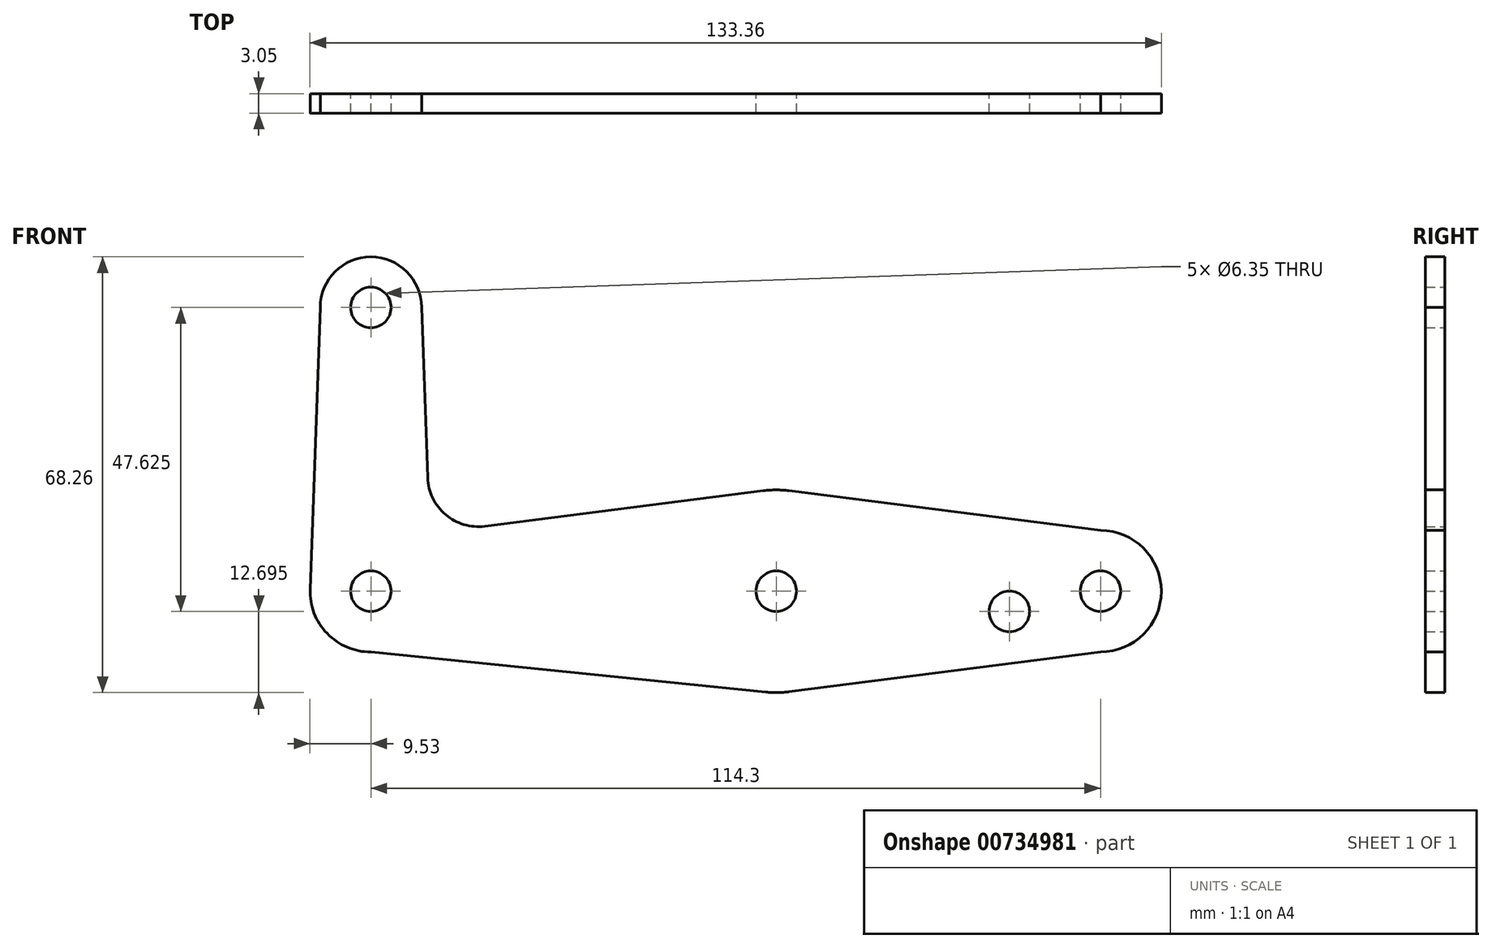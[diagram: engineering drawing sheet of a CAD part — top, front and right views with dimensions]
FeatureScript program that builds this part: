
annotation { "Feature Type Name" : "Feature", "Feature Type Description" : "" }
export const myFeature = defineFeature(function(context is Context, id is Id, definition is map)
    precondition{}
    {
        {
            var Q0;
            Q0=qCreatedBy(makeId("Front.planeOp"),FACE);
            var sketch = newSketch(context, id + "F0", { "sketchPlane" : qUnion([Q0])});
            skLineSegment(sketch, "E0", {"start": v(0, 0) * mm, "end": v(0, 44.45) * mm, "construction": true});
            skLineSegment(sketch, "E1", {"start": v(0, 0) * mm, "end": v(114.3, 0) * mm, "construction": true});
            skCircle(sketch, "E2", {"center": v(0, 44.45) * mm, "radius": 7.94 * mm});
            skCircle(sketch, "E3", {"center": v(0, 0) * mm, "radius": 9.53 * mm});
            skCircle(sketch, "E4", {"center": v(114.3, 0) * mm, "radius": 9.53 * mm});
            skCircle(sketch, "E5", {"center": v(63.5, 0) * mm, "radius": 15.88 * mm});
            skLineSegment(sketch, "E6", {"start": v(-7.94, 44.45) * mm, "end": v(-9.53, 0) * mm});
            skLineSegment(sketch, "E7", {"start": v(0, -9.52) * mm, "end": v(61.9, -15.8) * mm});
            skLineSegment(sketch, "E8", {"start": v(114.3, 9.53) * mm, "end": v(65.5, 15.75) * mm});
            skLineSegment(sketch, "E9", {"start": v(65.5, -15.75) * mm, "end": v(114.3, -9.53) * mm});
            skCircle(sketch, "E10", {"center": v(0, 44.45) * mm, "radius": 3.18 * mm});
            skCircle(sketch, "E11", {"center": v(0, 0) * mm, "radius": 3.18 * mm});
            skCircle(sketch, "E12", {"center": v(63.5, 0) * mm, "radius": 3.18 * mm});
            skCircle(sketch, "E13", {"center": v(114.3, 0) * mm, "radius": 3.18 * mm});
            skCircle(sketch, "E14", {"center": v(100.03, -3.18) * mm, "radius": 3.18 * mm});
            skLineSegment(sketch, "E15", {"start": v(7.94, 44.45) * mm, "end": v(8.9, 17.78) * mm});
            skLineSegment(sketch, "E16", {"start": v(17.84, 10.18) * mm, "end": v(61.5, 15.75) * mm});
            skPoint(sketch, "E17.newPointA", {"position": v(9.53, 0) * mm});
            skArc(sketch, "E17.filletArc", {"start": v(8.9, 17.78) * mm, "mid": v(11.7, 12) * mm, "end": v(17.84, 10.18) * mm});
            skSolve(sketch);
        }
        {
            var Q0;
            Q0 = qSketchRegion(id + "F0", true);
            extrude(context, id + "F1", {"entities" : qUnion([Q0]), "depth" : 3.05 * mm, "offsetDistance" : 25.4 * mm});
        }
    });
